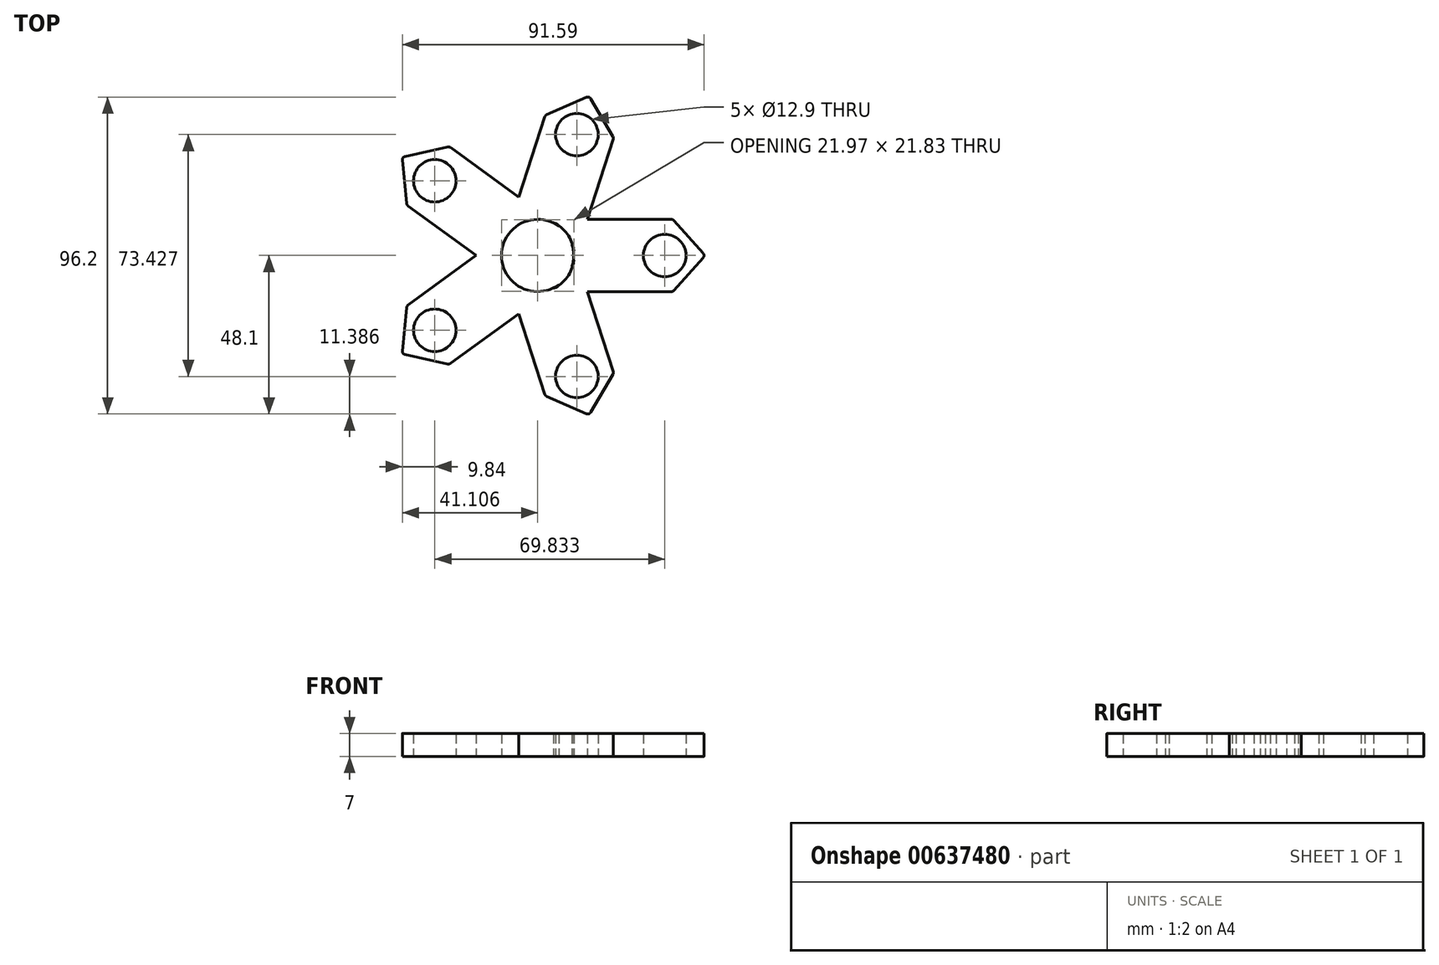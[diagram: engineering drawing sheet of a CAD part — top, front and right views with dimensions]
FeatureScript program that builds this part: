
annotation { "Feature Type Name" : "Feature", "Feature Type Description" : "" }
export const myFeature = defineFeature(function(context is Context, id is Id, definition is map)
    precondition{}
    {
        {
            var Q0;
            Q0=qCreatedBy(makeId("Top.planeOp"),FACE);
            var sketch = newSketch(context, id + "F0", { "sketchPlane" : qUnion([Q0])});
            skCircle(sketch, "E0", {"center": v(0, 0) * mm, "radius": 11.12 * mm});
            skCircle(sketch, "E1", {"center": v(0, 0) * mm, "radius": 10.95 * mm});
            skLineSegment(sketch, "E2", {"start": v(0, 10.95) * mm, "end": v(40.68, 10.95) * mm});
            skCircle(sketch, "E3", {"center": v(38.6, 0) * mm, "radius": 6.45 * mm});
            skLineSegment(sketch, "E4", {"start": v(41.43, 10.61) * mm, "end": v(50.27, 0.66) * mm});
            skLineSegment(sketch, "E5.MirrorCS", {"start": v(0, -10.95) * mm, "end": v(40.68, -10.95) * mm});
            skLineSegment(sketch, "E6.MirrorCS", {"start": v(41.43, -10.61) * mm, "end": v(50.27, -0.66) * mm});
            skLineSegment(sketch, "E7.1.0", {"start": v(22.9, 36.12) * mm, "end": v(16.17, 47.6) * mm});
            skLineSegment(sketch, "E7.1.1", {"start": v(2.7, 42.68) * mm, "end": v(14.9, 48.02) * mm});
            skLineSegment(sketch, "E7.1.2", {"start": v(-10.41, 3.38) * mm, "end": v(2.16, 42.07) * mm});
            skCircle(sketch, "E7.1.3", {"center": v(11.93, 36.71) * mm, "radius": 6.45 * mm});
            skLineSegment(sketch, "E7.1.5", {"start": v(10.41, -3.38) * mm, "end": v(22.98, 35.3) * mm});
            skLineSegment(sketch, "E7.2.0", {"start": v(-27.28, 32.94) * mm, "end": v(-40.28, 30.09) * mm});
            skLineSegment(sketch, "E7.2.1", {"start": v(-39.75, 15.76) * mm, "end": v(-41.06, 29.01) * mm});
            skLineSegment(sketch, "E7.2.2", {"start": v(-6.44, -8.86) * mm, "end": v(-39.35, 15.05) * mm});
            skCircle(sketch, "E7.2.3", {"center": v(-31.23, 22.7) * mm, "radius": 6.45 * mm});
            skLineSegment(sketch, "E7.2.5", {"start": v(6.44, 8.86) * mm, "end": v(-26.48, 32.77) * mm});
            skLineSegment(sketch, "E8.3.3.0", {"start": v(-27.28, -32.94) * mm, "end": v(-40.28, -30.09) * mm});
            skLineSegment(sketch, "E8.6.3.0", {"start": v(6.44, -8.86) * mm, "end": v(-26.48, -32.77) * mm});
            skCircle(sketch, "E8.9.3.0", {"center": v(-31.23, -22.7) * mm, "radius": 6.45 * mm});
            skLineSegment(sketch, "E8.13.3.0", {"start": v(-6.44, 8.86) * mm, "end": v(-39.35, -15.05) * mm});
            skLineSegment(sketch, "E8.14.3.0", {"start": v(-39.75, -15.76) * mm, "end": v(-41.06, -29.01) * mm});
            skLineSegment(sketch, "E8.3.4.0", {"start": v(22.9, -36.12) * mm, "end": v(16.17, -47.6) * mm});
            skLineSegment(sketch, "E8.6.4.0", {"start": v(10.41, 3.38) * mm, "end": v(22.98, -35.3) * mm});
            skCircle(sketch, "E8.9.4.0", {"center": v(11.93, -36.71) * mm, "radius": 6.45 * mm});
            skLineSegment(sketch, "E8.13.4.0", {"start": v(-10.41, -3.38) * mm, "end": v(2.16, -42.07) * mm});
            skLineSegment(sketch, "E8.14.4.0", {"start": v(2.7, -42.68) * mm, "end": v(14.9, -48.02) * mm});
            skPoint(sketch, "E9.visualSharp", {"position": v(50.86, 0) * mm});
            skArc(sketch, "E9.filletArc", {"start": v(50.27, -0.66) * mm, "mid": v(50.52, 0) * mm, "end": v(50.27, 0.66) * mm});
            skPoint(sketch, "E10.visualSharp", {"position": v(41.13, 10.95) * mm});
            skArc(sketch, "E10.filletArc", {"start": v(41.43, 10.61) * mm, "mid": v(41.1, 10.86) * mm, "end": v(40.68, 10.95) * mm});
            skPoint(sketch, "E11.visualSharp", {"position": v(41.13, -10.95) * mm});
            skArc(sketch, "E11.filletArc", {"start": v(40.68, -10.95) * mm, "mid": v(41.1, -10.86) * mm, "end": v(41.43, -10.61) * mm});
            skPoint(sketch, "E12.visualSharp", {"position": v(2.3, 42.5) * mm});
            skArc(sketch, "E12.filletArc", {"start": v(2.7, 42.68) * mm, "mid": v(2.37, 42.44) * mm, "end": v(2.16, 42.07) * mm});
            skPoint(sketch, "E13.visualSharp", {"position": v(15.72, 48.37) * mm});
            skArc(sketch, "E13.filletArc", {"start": v(16.17, 47.6) * mm, "mid": v(15.61, 48.05) * mm, "end": v(14.9, 48.02) * mm});
            skPoint(sketch, "E14.visualSharp", {"position": v(23.12, 35.73) * mm});
            skArc(sketch, "E14.filletArc", {"start": v(22.98, 35.3) * mm, "mid": v(23.03, 35.72) * mm, "end": v(22.9, 36.12) * mm});
            skPoint(sketch, "E15.visualSharp", {"position": v(-26.84, 33.03) * mm});
            skArc(sketch, "E15.filletArc", {"start": v(-26.48, 32.77) * mm, "mid": v(-26.86, 32.94) * mm, "end": v(-27.28, 32.94) * mm});
            skPoint(sketch, "E16.visualSharp", {"position": v(-41.15, 29.9) * mm});
            skArc(sketch, "E16.filletArc", {"start": v(-40.28, 30.09) * mm, "mid": v(-40.88, 29.7) * mm, "end": v(-41.06, 29.01) * mm});
            skPoint(sketch, "E17.visualSharp", {"position": v(-39.71, 15.32) * mm});
            skArc(sketch, "E17.filletArc", {"start": v(-39.75, 15.76) * mm, "mid": v(-39.63, 15.37) * mm, "end": v(-39.35, 15.05) * mm});
            skPoint(sketch, "E18.visualSharp", {"position": v(-39.71, -15.32) * mm});
            skArc(sketch, "E18.filletArc", {"start": v(-39.35, -15.05) * mm, "mid": v(-39.63, -15.37) * mm, "end": v(-39.75, -15.76) * mm});
            skPoint(sketch, "E19.visualSharp", {"position": v(-41.15, -29.9) * mm});
            skArc(sketch, "E19.filletArc", {"start": v(-41.06, -29.01) * mm, "mid": v(-40.88, -29.7) * mm, "end": v(-40.28, -30.09) * mm});
            skPoint(sketch, "E20.visualSharp", {"position": v(-26.84, -33.03) * mm});
            skArc(sketch, "E20.filletArc", {"start": v(-27.28, -32.94) * mm, "mid": v(-26.86, -32.94) * mm, "end": v(-26.48, -32.77) * mm});
            skPoint(sketch, "E21.visualSharp", {"position": v(2.3, -42.5) * mm});
            skArc(sketch, "E21.filletArc", {"start": v(2.16, -42.07) * mm, "mid": v(2.37, -42.44) * mm, "end": v(2.7, -42.68) * mm});
            skPoint(sketch, "E22.visualSharp", {"position": v(15.72, -48.37) * mm});
            skArc(sketch, "E22.filletArc", {"start": v(14.9, -48.02) * mm, "mid": v(15.61, -48.05) * mm, "end": v(16.17, -47.6) * mm});
            skPoint(sketch, "E23.visualSharp", {"position": v(23.12, -35.73) * mm});
            skArc(sketch, "E23.filletArc", {"start": v(22.9, -36.12) * mm, "mid": v(23.03, -35.72) * mm, "end": v(22.98, -35.3) * mm});
            skSolve(sketch);
        }
        {
            var Q0;
            {var subQ3=sQuery(id+"F0.wireOp",EDGE,"E7.1.5");var subQ7=sQuery(id+"F0.wireOp",EDGE,"E2");var subQ9=makeQuery(id+"F0.imprint","INTERSECT",VERTEX,{"derivedFrom":[subQ7,subQ3]});Q0=makeQuery(id+"F0.imprint","IMPRINT",FACE,{"disambiguationData":[TD([[makeQuery(id+"F0.imprint","IMPRINT",EDGE,{"disambiguationData":[TD([[subQ9,1.0]])],"derivedFrom":subQ7}),-1.0]])]});}
            var Q1;
            Q1=makeQuery(id+"F0.imprint","IMPRINT",FACE,{"disambiguationData":[TD([[makeQuery(id+"F0.imprint","IMPRINT",EDGE,{"derivedFrom":sQuery(id+"F0.wireOp",EDGE,"E3")}),-1.0]])]});
            var Q2;
            Q2=makeQuery(id+"F0.imprint","IMPRINT",FACE,{"disambiguationData":[TD([[makeQuery(id+"F0.imprint","IMPRINT",EDGE,{"derivedFrom":sQuery(id+"F0.wireOp",EDGE,"E8.3.3.0")}),-1.0]])]});
            var Q3;
            Q3=makeQuery(id+"F0.imprint","IMPRINT",FACE,{"disambiguationData":[TD([[makeQuery(id+"F0.imprint","IMPRINT",EDGE,{"derivedFrom":sQuery(id+"F0.wireOp",EDGE,"E7.1.0")}),1.0]])]});
            var Q4;
            Q4=makeQuery(id+"F0.imprint","IMPRINT",FACE,{"disambiguationData":[TD([[makeQuery(id+"F0.imprint","IMPRINT",EDGE,{"derivedFrom":sQuery(id+"F0.wireOp",EDGE,"E0")}),-1.0]])]});
            var Q5;
            {var subQ0=sQuery(id+"F0.wireOp",EDGE,"E1");var subQ7=sQuery(id+"F0.wireOp",EDGE,"E2");var subQ9=makeQuery(id+"F0.imprint","INTERSECT",VERTEX,{"derivedFrom":[subQ7,subQ0]});Q5=makeQuery(id+"F0.imprint","IMPRINT",FACE,{"disambiguationData":[TD([[makeQuery(id+"F0.imprint","IMPRINT",EDGE,{"disambiguationData":[TD([[subQ9,-1.0]])],"derivedFrom":subQ7}),1.0]])]});}
            var Q6;
            {var subQ5=sQuery(id+"F0.wireOp",EDGE,"E1");var subQ6=sQuery(id+"F0.wireOp",EDGE,"E5.MirrorCS");var subQ7=makeQuery(id+"F0.imprint","INTERSECT",VERTEX,{"derivedFrom":[subQ6,subQ5]});Q6=makeQuery(id+"F0.imprint","IMPRINT",FACE,{"disambiguationData":[TD([[makeQuery(id+"F0.imprint","IMPRINT",EDGE,{"disambiguationData":[TD([[subQ7,-1.0]])],"derivedFrom":subQ6}),-1.0]])]});}
            var Q7;
            Q7=makeQuery(id+"F0.imprint","IMPRINT",FACE,{"disambiguationData":[TD([[makeQuery(id+"F0.imprint","IMPRINT",EDGE,{"derivedFrom":sQuery(id+"F0.wireOp",EDGE,"E8.3.4.0")}),-1.0]])]});
            var Q8;
            Q8=makeQuery(id+"F0.imprint","IMPRINT",FACE,{"disambiguationData":[TD([[makeQuery(id+"F0.imprint","IMPRINT",EDGE,{"derivedFrom":sQuery(id+"F0.wireOp",EDGE,"E7.2.0")}),1.0]])]});
            var Q9;
            {var subQ0=sQuery(id+"F0.wireOp",EDGE,"E1");var subQ7=sQuery(id+"F0.wireOp",EDGE,"E7.1.2");var subQ9=makeQuery(id+"F0.imprint","INTERSECT",VERTEX,{"derivedFrom":[subQ7,subQ0]});Q9=makeQuery(id+"F0.imprint","IMPRINT",FACE,{"disambiguationData":[TD([[makeQuery(id+"F0.imprint","IMPRINT",EDGE,{"disambiguationData":[TD([[subQ9,-1.0]])],"derivedFrom":subQ7}),1.0]])]});}
            var Q10;
            {var subQ0=sQuery(id+"F0.wireOp",EDGE,"E8.6.4.0");var subQ1=sQuery(id+"F0.wireOp",EDGE,"E5.MirrorCS");var subQ2=makeQuery(id+"F0.imprint","INTERSECT",VERTEX,{"derivedFrom":[subQ1,subQ0]});Q10=makeQuery(id+"F0.imprint","IMPRINT",FACE,{"disambiguationData":[TD([[makeQuery(id+"F0.imprint","IMPRINT",EDGE,{"disambiguationData":[TD([[subQ2,1.0]])],"derivedFrom":subQ1}),1.0]])]});}
            var Q11;
            {var subQ0=sQuery(id+"F0.wireOp",EDGE,"E1");var subQ1=sQuery(id+"F0.wireOp",EDGE,"E7.1.2");var subQ2=makeQuery(id+"F0.imprint","INTERSECT",VERTEX,{"derivedFrom":[subQ1,subQ0]});Q11=makeQuery(id+"F0.imprint","IMPRINT",FACE,{"disambiguationData":[TD([[makeQuery(id+"F0.imprint","IMPRINT",EDGE,{"disambiguationData":[TD([[subQ2,-1.0]])],"derivedFrom":subQ1}),-1.0]])]});}
            var Q12;
            {var subQ0=sQuery(id+"F0.wireOp",EDGE,"E1");var subQ1=sQuery(id+"F0.wireOp",EDGE,"E7.1.5");var subQ2=makeQuery(id+"F0.imprint","INTERSECT",VERTEX,{"derivedFrom":[subQ1,subQ0]});Q12=makeQuery(id+"F0.imprint","IMPRINT",FACE,{"disambiguationData":[TD([[makeQuery(id+"F0.imprint","IMPRINT",EDGE,{"disambiguationData":[TD([[subQ2,-1.0]])],"derivedFrom":subQ1}),1.0]])]});}
            var Q13;
            {var subQ0=sQuery(id+"F0.wireOp",EDGE,"E1");var subQ1=sQuery(id+"F0.wireOp",EDGE,"E5.MirrorCS");var subQ2=makeQuery(id+"F0.imprint","INTERSECT",VERTEX,{"derivedFrom":[subQ1,subQ0]});Q13=makeQuery(id+"F0.imprint","IMPRINT",FACE,{"disambiguationData":[TD([[makeQuery(id+"F0.imprint","IMPRINT",EDGE,{"disambiguationData":[TD([[subQ2,-1.0]])],"derivedFrom":subQ1}),1.0]])]});}
            var Q14;
            {var subQ0=sQuery(id+"F0.wireOp",EDGE,"E1");var subQ1=sQuery(id+"F0.wireOp",EDGE,"E7.2.2");var subQ2=makeQuery(id+"F0.imprint","INTERSECT",VERTEX,{"derivedFrom":[subQ1,subQ0]});Q14=makeQuery(id+"F0.imprint","IMPRINT",FACE,{"disambiguationData":[TD([[makeQuery(id+"F0.imprint","IMPRINT",EDGE,{"disambiguationData":[TD([[subQ2,-1.0]])],"derivedFrom":subQ1}),-1.0]])]});}
            var Q15;
            {var subQ0=sQuery(id+"F0.wireOp",EDGE,"E1");var subQ1=sQuery(id+"F0.wireOp",EDGE,"E2");var subQ2=makeQuery(id+"F0.imprint","INTERSECT",VERTEX,{"derivedFrom":[subQ1,subQ0]});Q15=makeQuery(id+"F0.imprint","IMPRINT",FACE,{"disambiguationData":[TD([[makeQuery(id+"F0.imprint","IMPRINT",EDGE,{"disambiguationData":[TD([[subQ2,-1.0]])],"derivedFrom":subQ1}),-1.0]])]});}
            var Q16;
            {var subQ0=sQuery(id+"F0.wireOp",EDGE,"E0");var subQ1=sQuery(id+"F0.wireOp",EDGE,"E7.1.2");var subQ2=makeQuery(id+"F0.imprint","INTERSECT",VERTEX,{"derivedFrom":[subQ1,subQ0]});Q16=makeQuery(id+"F0.imprint","IMPRINT",FACE,{"disambiguationData":[TD([[makeQuery(id+"F0.imprint","IMPRINT",EDGE,{"disambiguationData":[TD([[subQ2,-1.0]])],"derivedFrom":subQ1}),1.0]])]});}
            var Q17;
            {var subQ3=sQuery(id+"F0.wireOp",EDGE,"E0");var subQ7=sQuery(id+"F0.wireOp",EDGE,"E2");var subQ9=makeQuery(id+"F0.imprint","INTERSECT",VERTEX,{"derivedFrom":[subQ7,subQ3]});Q17=makeQuery(id+"F0.imprint","IMPRINT",FACE,{"disambiguationData":[TD([[makeQuery(id+"F0.imprint","IMPRINT",EDGE,{"disambiguationData":[TD([[subQ9,-1.0]])],"derivedFrom":subQ7}),1.0]])]});}
            var Q18;
            {var subQ0=sQuery(id+"F0.wireOp",EDGE,"E0");var subQ1=sQuery(id+"F0.wireOp",EDGE,"E5.MirrorCS");var subQ2=makeQuery(id+"F0.imprint","INTERSECT",VERTEX,{"derivedFrom":[subQ1,subQ0]});Q18=makeQuery(id+"F0.imprint","IMPRINT",FACE,{"disambiguationData":[TD([[makeQuery(id+"F0.imprint","IMPRINT",EDGE,{"disambiguationData":[TD([[subQ2,-1.0]])],"derivedFrom":subQ1}),-1.0]])]});}
            extrude(context, id + "F1", {"entities" : qUnion([Q0, Q1, Q2, Q3, Q4, Q5, Q6, Q7, Q8, Q9, Q10, Q11, Q12, Q13, Q14, Q15, Q16, Q17, Q18]), "depth" : 7 * mm, "offsetDistance" : 25 * mm});
        }
    });
